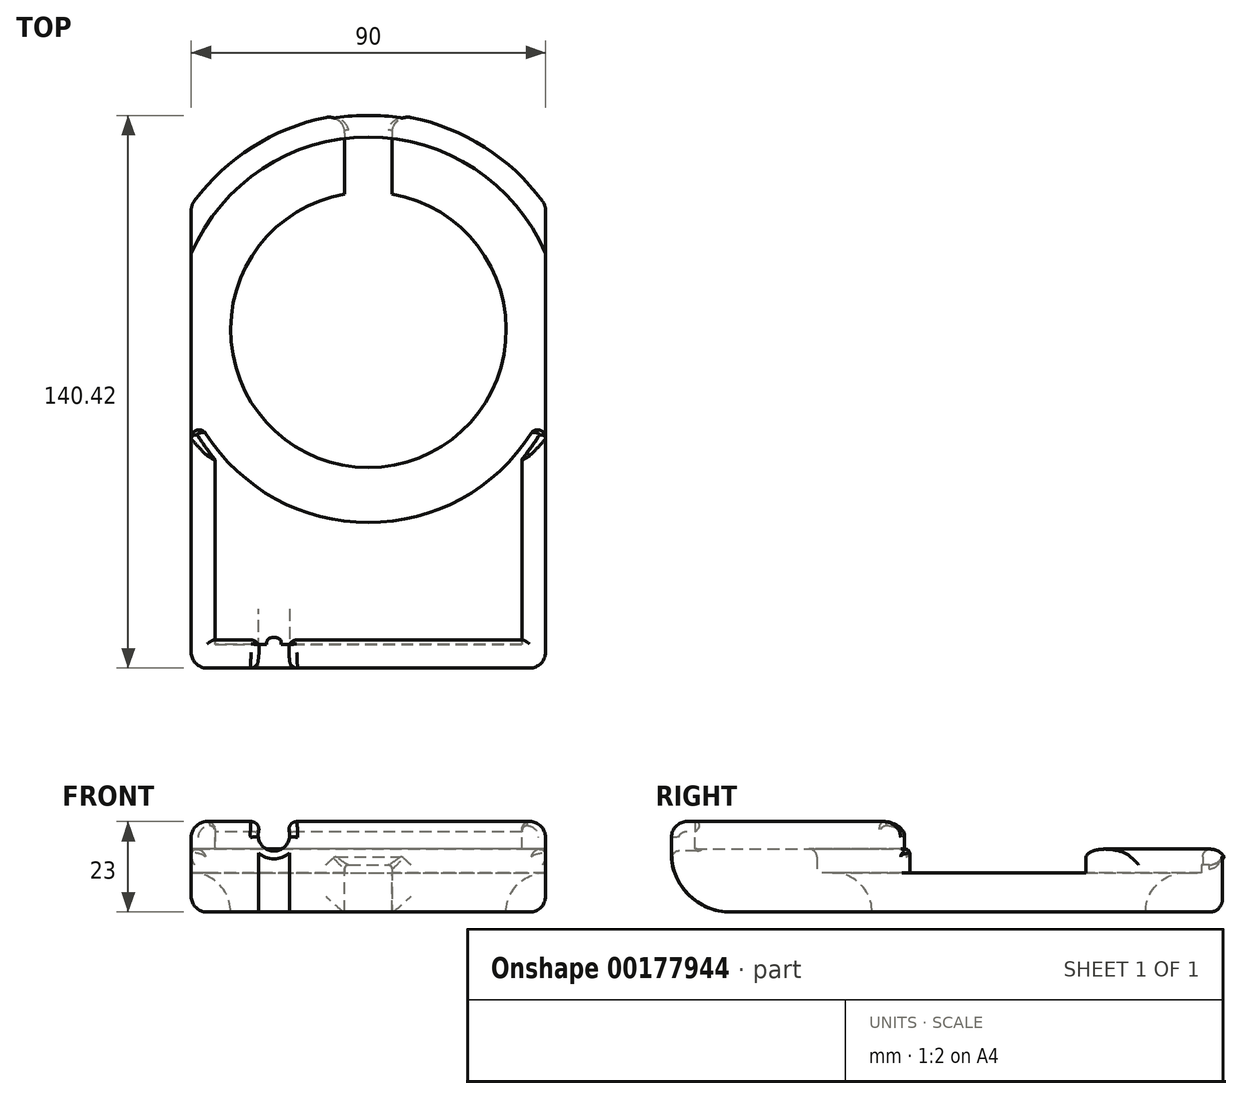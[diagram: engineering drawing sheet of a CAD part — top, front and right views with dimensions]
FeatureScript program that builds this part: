
annotation { "Feature Type Name" : "Feature", "Feature Type Description" : "" }
export const myFeature = defineFeature(function(context is Context, id is Id, definition is map)
    precondition{}
    {
        {
            var Q0;
            Q0=qCreatedBy(makeId("Top.planeOp"),FACE);
            var sketch = newSketch(context, id + "F0", { "sketchPlane" : qUnion([Q0])});
            skCircle(sketch, "E0", {"center": v(0, 0) * mm, "radius": 35 * mm});
            skLineSegment(sketch, "E1.bottom", {"start": v(45, -80) * mm, "end": v(-45, -80) * mm});
            skLineSegment(sketch, "E1.top", {"start": v(45, 80) * mm, "end": v(-45, 80) * mm});
            skLineSegment(sketch, "E1.left", {"start": v(45, -80) * mm, "end": v(45, 80) * mm});
            skLineSegment(sketch, "E1.right", {"start": v(-45, -80) * mm, "end": v(-45, 80) * mm});
            skSolve(sketch);
        }
        {
            var Q0;
            Q0 = qSketchRegion(id + "F0", true);
            extrude(context, id + "F1", {"entities" : qUnion([Q0]), "depth" : 10 * mm});
        }
        {
            var Q0;
            Q0=makeQuery(id+"F1.opExtrude","CAP_EDGE",EDGE,{"disambiguationData":[OSD([sQuery(id+"F0.wireOp",EDGE,"E0")])],"isStart":false});
            fillet(context, id + "F2", {"entities" : qUnion([Q0]), "radius" : 10 * mm, "tangentPropagation" : true, "allowEdgeOverflow" : false});
        }
        {
            var Q0;
            Q0=makeQuery(id+"F2.opFillet","SPLIT",FACE,{"disambiguationData":[OD(1.0)],"derivedFrom":makeQuery(id+"F1.opExtrude","CAP_FACE",FACE,{"disambiguationData":[OSD([sQuery(id+"F0.wireOp",EDGE,"E0"),sQuery(id+"F0.wireOp",EDGE,"E1.bottom"),sQuery(id+"F0.wireOp",EDGE,"E1.top"),sQuery(id+"F0.wireOp",EDGE,"E1.left"),sQuery(id+"F0.wireOp",EDGE,"E1.right")])],"isStart":false})});
            var sketch = newSketch(context, id + "F3", { "sketchPlane" : qUnion([Q0])});
            skCircle(sketch, "E2", {"center": v(0, 0) * mm, "radius": 49 * mm});
            skLineSegment(sketch, "E3.bottom", {"start": v(45, -80) * mm, "end": v(-45, -80) * mm});
            skLineSegment(sketch, "E3.top", {"start": v(45, 80) * mm, "end": v(-45, 80) * mm});
            skLineSegment(sketch, "E3.left", {"start": v(45, -80) * mm, "end": v(45, 80) * mm});
            skLineSegment(sketch, "E3.right", {"start": v(-45, -80) * mm, "end": v(-45, 80) * mm});
            skSolve(sketch);
        }
        {
            var Q0;
            {var subQ5=sQuery(id+"F3.wireOp",EDGE,"E3.top");Q0=makeQuery(id+"F3.imprint","IMPRINT",FACE,{"disambiguationData":[TD([[makeQuery(id+"F3.imprint","IMPRINT",EDGE,{"derivedFrom":subQ5}),1.0]])]});}
            var Q1;
            {var subQ5=sQuery(id+"F3.wireOp",EDGE,"E3.bottom");Q1=makeQuery(id+"F3.imprint","IMPRINT",FACE,{"disambiguationData":[TD([[makeQuery(id+"F3.imprint","IMPRINT",EDGE,{"derivedFrom":subQ5}),-1.0]])]});}
            extrude(context, id + "F4", {"entities" : qUnion([Q0, Q1]), "operationType" : NewBodyOperationType.ADD, "depth" : 6 * mm});
        }
        {
            var Q0;
            {var subQ0=sQuery(id+"F3.wireOp",EDGE,"E2");Q0=makeQuery(id+"F4.opExtrude","CAP_EDGE",EDGE,{"disambiguationData":[OSD([subQ0]),TDD([makeQuery(id+"F3.imprint","IMPRINT",EDGE,{"disambiguationData":[TD([[makeQuery(id+"F3.imprint","INTERSECT",VERTEX,{"disambiguationData":[OD(0.0)],"derivedFrom":[subQ0,sQuery(id+"F3.wireOp",EDGE,"E3.right")]}),1.0]])],"derivedFrom":subQ0})])],"isStart":true});}
            var Q1;
            {var subQ0=sQuery(id+"F3.wireOp",EDGE,"E2");Q1=makeQuery(id+"F4.opExtrude","CAP_EDGE",EDGE,{"disambiguationData":[OSD([subQ0]),TDD([makeQuery(id+"F3.imprint","IMPRINT",EDGE,{"disambiguationData":[TD([[makeQuery(id+"F3.imprint","INTERSECT",VERTEX,{"disambiguationData":[OD(0.0)],"derivedFrom":[subQ0,sQuery(id+"F3.wireOp",EDGE,"E3.right")]}),1.0]])],"derivedFrom":subQ0})])],"isStart":false});}
            var Q2;
            {var subQ0=sQuery(id+"F3.wireOp",EDGE,"E2");Q2=makeQuery(id+"F4.opExtrude","CAP_EDGE",EDGE,{"disambiguationData":[OSD([subQ0]),TDD([makeQuery(id+"F3.imprint","IMPRINT",EDGE,{"disambiguationData":[TD([[makeQuery(id+"F3.imprint","INTERSECT",VERTEX,{"disambiguationData":[OD(1.0)],"derivedFrom":[subQ0,sQuery(id+"F3.wireOp",EDGE,"E3.right")]}),-1.0]])],"derivedFrom":subQ0})])],"isStart":true});}
            var Q3;
            {var subQ0=sQuery(id+"F3.wireOp",EDGE,"E2");Q3=makeQuery(id+"F4.opExtrude","CAP_EDGE",EDGE,{"disambiguationData":[OSD([subQ0]),TDD([makeQuery(id+"F3.imprint","IMPRINT",EDGE,{"disambiguationData":[TD([[makeQuery(id+"F3.imprint","INTERSECT",VERTEX,{"disambiguationData":[OD(1.0)],"derivedFrom":[subQ0,sQuery(id+"F3.wireOp",EDGE,"E3.right")]}),-1.0]])],"derivedFrom":subQ0})])],"isStart":false});}
            fillet(context, id + "F5", {"entities" : qUnion([Q0, Q1, Q2, Q3]), "radius" : 2 * mm, "tangentPropagation" : true, "allowEdgeOverflow" : false});
        }
        {
            var Q0;
            Q0=makeQuery(id+"F4.opExtrude","CAP_FACE",FACE,{"disambiguationData":[OSD([sQuery(id+"F3.wireOp",EDGE,"E2"),sQuery(id+"F3.wireOp",EDGE,"E3.top"),sQuery(id+"F3.wireOp",EDGE,"E3.left"),sQuery(id+"F3.wireOp",EDGE,"E3.right")])],"isStart":false});
            var sketch = newSketch(context, id + "F6", { "sketchPlane" : qUnion([Q0])});
            skCircle(sketch, "E4", {"center": v(0, 0) * mm, "radius": 55 * mm});
            skLineSegment(sketch, "E5", {"start": v(-45, 31.62) * mm, "end": v(-45, 80) * mm});
            skLineSegment(sketch, "E6", {"start": v(-45, 80) * mm, "end": v(45, 80) * mm});
            skLineSegment(sketch, "E7", {"start": v(45, 80) * mm, "end": v(45, 31.62) * mm});
            skSolve(sketch);
        }
        {
            var Q0;
            {var subQ0=sQuery(id+"F6.wireOp",EDGE,"E5");Q0=makeQuery(id+"F6.imprint","IMPRINT",FACE,{"disambiguationData":[TD([[makeQuery(id+"F6.imprint","IMPRINT",EDGE,{"derivedFrom":subQ0}),-1.0]])]});}
            extrude(context, id + "F7", {"entities" : qUnion([Q0]), "operationType" : NewBodyOperationType.REMOVE, "endBound" : BoundingType.UP_TO_NEXT, "oppositeDirection" : true, "depth" : 25 * mm});
        }
        {
            var Q0;
            Q0=makeQuery(id+"F4.opExtrude","CAP_FACE",FACE,{"disambiguationData":[OSD([sQuery(id+"F3.wireOp",EDGE,"E2"),sQuery(id+"F3.wireOp",EDGE,"E3.bottom"),sQuery(id+"F3.wireOp",EDGE,"E3.left"),sQuery(id+"F3.wireOp",EDGE,"E3.right")])],"isStart":false});
            var sketch = newSketch(context, id + "F8", { "sketchPlane" : qUnion([Q0])});
            skLineSegment(sketch, "E8.bottom", {"start": v(39, -80) * mm, "end": v(-39, -80) * mm});
            skLineSegment(sketch, "E8.top", {"start": v(39, 80) * mm, "end": v(-39, 80) * mm});
            skLineSegment(sketch, "E8.left", {"start": v(39, -80) * mm, "end": v(39, 80) * mm});
            skLineSegment(sketch, "E8.right", {"start": v(-39, -80) * mm, "end": v(-39, 80) * mm});
            skPoint(sketch, "E8.middle", {"position": v(0, 0) * mm});
            skLineSegment(sketch, "E9.bottom", {"start": v(45, -86) * mm, "end": v(-45, -86) * mm});
            skLineSegment(sketch, "E9.top", {"start": v(45, 86) * mm, "end": v(-45, 86) * mm});
            skLineSegment(sketch, "E9.left", {"start": v(45, -86) * mm, "end": v(45, 86) * mm});
            skLineSegment(sketch, "E9.right", {"start": v(-45, -86) * mm, "end": v(-45, 86) * mm});
            skArc(sketch, "E10", {"start": v(-45, -24) * mm, "mid": v(0, -51) * mm, "end": v(45, -24) * mm});
            skSolve(sketch);
        }
        {
            var Q0;
            {var subQ1=makeQuery(id+"F4.opExtrude","CAP_EDGE",EDGE,{"disambiguationData":[OSD([sQuery(id+"F3.wireOp",EDGE,"E3.bottom")])],"isStart":false});var subQ5=sQuery(id+"F8.wireOp",EDGE,"E9.left");var subQ7=makeQuery(id+"F8.imprint","INTERSECT",VERTEX,{"derivedFrom":[subQ1,subQ5]});Q0=makeQuery(id+"F8.imprint","IMPRINT",FACE,{"disambiguationData":[TD([[makeQuery(id+"F8.imprint","IMPRINT",EDGE,{"disambiguationData":[TD([[subQ7,-1.0]])],"derivedFrom":subQ5}),1.0]])]});}
            var Q1;
            {var subQ1=makeQuery(id+"F4.opExtrude","CAP_EDGE",EDGE,{"disambiguationData":[OSD([sQuery(id+"F3.wireOp",EDGE,"E3.bottom")])],"isStart":false});var subQ5=sQuery(id+"F8.wireOp",EDGE,"E9.right");var subQ6=makeQuery(id+"F8.imprint","INTERSECT",VERTEX,{"derivedFrom":[subQ1,subQ5]});Q1=makeQuery(id+"F8.imprint","IMPRINT",FACE,{"disambiguationData":[TD([[makeQuery(id+"F8.imprint","IMPRINT",EDGE,{"disambiguationData":[TD([[subQ6,-1.0]])],"derivedFrom":subQ5}),-1.0]])]});}
            extrude(context, id + "F9", {"entities" : qUnion([Q0, Q1]), "operationType" : NewBodyOperationType.ADD, "depth" : 7 * mm});
        }
        {
            var Q0;
            Q0=qCreatedBy(makeId("Right.planeOp"),FACE);
            var sketch = newSketch(context, id + "F10", { "sketchPlane" : qUnion([Q0])});
            skLineSegment(sketch, "E11", {"start": v(-64.77, -48.06) * mm, "end": v(-70.53, -49.87) * mm});
            skLineSegment(sketch, "E12", {"start": v(-85.96, 0) * mm, "end": v(-85.96, 23) * mm});
            skLineSegment(sketch, "E13", {"start": v(-79.96, 0) * mm, "end": v(-79.96, 20.33) * mm});
            skLineSegment(sketch, "E14", {"start": v(-79.96, 0) * mm, "end": v(-85.96, 0) * mm});
            skLineSegment(sketch, "E15", {"start": v(-85.96, 23) * mm, "end": v(-77.63, 23) * mm});
            skLineSegment(sketch, "E16", {"start": v(-77.63, 23) * mm, "end": v(-79.96, 20.33) * mm});
            skSolve(sketch);
        }
        {
            var Q0;
            Q0 = qSketchRegion(id + "F10", true);
            extrude(context, id + "F11", {"entities" : qUnion([Q0]), "operationType" : NewBodyOperationType.ADD, "depth" : 45 * mm, "hasSecondDirection" : true, "secondDirectionOppositeDirection" : true, "secondDirectionDepth" : 45 * mm});
        }
        {
            var Q0;
            Q0=makeQuery(id+"F11.opExtrude","SWEPT_FACE",FACE,{"disambiguationData":[OSD([sQuery(id+"F10.wireOp",EDGE,"E12")])]});
            var sketch = newSketch(context, id + "F12", { "sketchPlane" : qUnion([Q0])});
            skCircle(sketch, "E17", {"center": v(-24, 19.53) * mm, "radius": 4 * mm});
            skSolve(sketch);
        }
        {
            var Q0;
            Q0 = qSketchRegion(id + "F12", true);
            extrude(context, id + "F13", {"entities" : qUnion([Q0]), "operationType" : NewBodyOperationType.REMOVE, "oppositeDirection" : true, "depth" : 8.5 * mm});
        }
        {
            var Q0;
            Q0=qCreatedBy(makeId("Front.planeOp"),FACE);
            var sketch = newSketch(context, id + "F14", { "sketchPlane" : qUnion([Q0])});
            skLineSegment(sketch, "E18.bottom", {"start": v(-6, 0) * mm, "end": v(6, 0) * mm});
            skLineSegment(sketch, "E18.top", {"start": v(-6, 12) * mm, "end": v(6, 12) * mm});
            skLineSegment(sketch, "E18.left", {"start": v(-6, 0) * mm, "end": v(-6, 12) * mm});
            skLineSegment(sketch, "E18.right", {"start": v(6, 0) * mm, "end": v(6, 12) * mm});
            skPoint(sketch, "E18.middle", {"position": v(0, 6) * mm});
            skSolve(sketch);
        }
        {
            var Q0;
            Q0 = qSketchRegion(id + "F14", true);
            extrude(context, id + "F15", {"entities" : qUnion([Q0]), "operationType" : NewBodyOperationType.REMOVE, "endBound" : BoundingType.THROUGH_ALL, "oppositeDirection" : true, "depth" : 25 * mm});
        }
        {
            var Q0;
            Q0=makeQuery(id+"F7.boolean.opBoolean","COPY",FACE,{"derivedFrom":makeQuery(id+"F7.opExtrude","SWEPT_FACE",FACE,{"disambiguationData":[OSD([sQuery(id+"F6.wireOp",EDGE,"E4")])]})});
            var Q1;
            Q1=makeQuery(id+"F15.boolean.opBoolean","COPY",EDGE,{"derivedFrom":makeQuery(id+"F15.opExtrude","SWEPT_EDGE",EDGE,{"disambiguationData":[OSD([sQuery(id+"F14.wireOp",EDGE,"E18.bottom"),sQuery(id+"F14.wireOp",EDGE,"E18.left")])]})});
            var Q2;
            Q2=makeQuery(id+"F15.boolean.opBoolean","COPY",EDGE,{"derivedFrom":makeQuery(id+"F15.opExtrude","SWEPT_EDGE",EDGE,{"disambiguationData":[OSD([sQuery(id+"F14.wireOp",EDGE,"E18.bottom"),sQuery(id+"F14.wireOp",EDGE,"E18.right")])]})});
            var Q3;
            Q3=makeQuery(id+"F11.boolean.opBoolean","MERGE",EDGE,{"derivedFrom":[makeQuery(id+"F1.opExtrude","CAP_EDGE",EDGE,{"disambiguationData":[OSD([sQuery(id+"F0.wireOp",EDGE,"E1.left")])],"isStart":true}),makeQuery(id+"F11.opExtrude","CAP_EDGE",EDGE,{"disambiguationData":[OSD([sQuery(id+"F10.wireOp",EDGE,"E14")])],"isStart":false})]});
            var Q4;
            Q4=makeQuery(id+"F11.boolean.opBoolean","MERGE",EDGE,{"derivedFrom":[makeQuery(id+"F1.opExtrude","CAP_EDGE",EDGE,{"disambiguationData":[OSD([sQuery(id+"F0.wireOp",EDGE,"E1.right")])],"isStart":true}),makeQuery(id+"F11.opExtrude","CAP_EDGE",EDGE,{"disambiguationData":[OSD([sQuery(id+"F10.wireOp",EDGE,"E14")])],"isStart":true})]});
            var Q5;
            Q5=makeQuery(id+"F11.opExtrude","CAP_EDGE",EDGE,{"disambiguationData":[OSD([sQuery(id+"F10.wireOp",EDGE,"E12")])],"isStart":false});
            var Q6;
            Q6=makeQuery(id+"F11.opExtrude","CAP_EDGE",EDGE,{"disambiguationData":[OSD([sQuery(id+"F10.wireOp",EDGE,"E12")])],"isStart":true});
            var Q7;
            Q7=makeQuery(id+"F11.boolean.opBoolean","MERGE",EDGE,{"derivedFrom":[makeQuery(id+"F9.opExtrude","CAP_EDGE",EDGE,{"disambiguationData":[OSD([sQuery(id+"F8.wireOp",EDGE,"E9.right")])],"isStart":false}),makeQuery(id+"F11.opExtrude","CAP_EDGE",EDGE,{"disambiguationData":[OSD([sQuery(id+"F10.wireOp",EDGE,"E15")])],"isStart":true})]});
            var Q8;
            Q8=makeQuery(id+"F11.boolean.opBoolean","MERGE",EDGE,{"derivedFrom":[makeQuery(id+"F9.opExtrude","CAP_EDGE",EDGE,{"disambiguationData":[OSD([sQuery(id+"F8.wireOp",EDGE,"E9.left")])],"isStart":false}),makeQuery(id+"F11.opExtrude","CAP_EDGE",EDGE,{"disambiguationData":[OSD([sQuery(id+"F10.wireOp",EDGE,"E15")])],"isStart":false})]});
            var Q9;
            {var subQ5=sQuery(id+"F10.wireOp",EDGE,"E12");var subQ6=sQuery(id+"F10.wireOp",EDGE,"E15");Q9=makeQuery(id+"F13.boolean.opBoolean","SPLIT",EDGE,{"disambiguationData":[TD([makeQuery(id+"F1.opExtrude","SWEPT_FACE",FACE,{"disambiguationData":[OSD([sQuery(id+"F0.wireOp",EDGE,"E1.left")])]})])],"derivedFrom":makeQuery(id+"F11.opExtrude","SWEPT_EDGE",EDGE,{"disambiguationData":[OSD([subQ5,subQ6])]})});}
            var Q10;
            {var subQ5=sQuery(id+"F10.wireOp",EDGE,"E15");var subQ6=sQuery(id+"F10.wireOp",EDGE,"E12");Q10=makeQuery(id+"F13.boolean.opBoolean","SPLIT",EDGE,{"disambiguationData":[TD([makeQuery(id+"F1.opExtrude","SWEPT_FACE",FACE,{"disambiguationData":[OSD([sQuery(id+"F0.wireOp",EDGE,"E1.right")])]})])],"derivedFrom":makeQuery(id+"F11.opExtrude","SWEPT_EDGE",EDGE,{"disambiguationData":[OSD([subQ6,subQ5])]})});}
            var Q11;
            Q11=makeQuery(id+"F13.boolean.opBoolean","COPY",EDGE,{"derivedFrom":makeQuery(id+"F13.opExtrude","CAP_EDGE",EDGE,{"disambiguationData":[OSD([sQuery(id+"F12.wireOp",EDGE,"E17")])],"isStart":true})});
            fillet(context, id + "F16", {"entities" : qUnion([Q0, Q1, Q2, Q3, Q4, Q5, Q6, Q7, Q8, Q9, Q10, Q11]), "radius" : 4 * mm, "tangentPropagation" : true, "allowEdgeOverflow" : false});
        }
        {
            var Q0;
            {var subQ0=sQuery(id+"F8.wireOp",EDGE,"E10");var subQ1=sQuery(id+"F3.wireOp",EDGE,"E3.bottom");Q0=makeQuery(id+"F13.boolean.opBoolean","INTERSECT",EDGE,{"disambiguationData":[OD(1.0)],"derivedFrom":[makeQuery(id+"F11.boolean.opBoolean","MERGE",FACE,{"derivedFrom":[makeQuery(id+"F9.opExtrude","CAP_FACE",FACE,{"disambiguationData":[OSD([subQ1,sQuery(id+"F8.wireOp",EDGE,"E8.left"),sQuery(id+"F8.wireOp",EDGE,"E9.left"),subQ0])],"isStart":false}),makeQuery(id+"F9.opExtrude","CAP_FACE",FACE,{"disambiguationData":[OSD([subQ1,sQuery(id+"F8.wireOp",EDGE,"E8.right"),sQuery(id+"F8.wireOp",EDGE,"E9.right"),subQ0])],"isStart":false}),makeQuery(id+"F11.opExtrude","SWEPT_FACE",FACE,{"disambiguationData":[OSD([sQuery(id+"F10.wireOp",EDGE,"E15")])]})]}),makeQuery(id+"F13.opExtrude","SWEPT_FACE",FACE,{"disambiguationData":[OSD([sQuery(id+"F12.wireOp",EDGE,"E17")])]})]});}
            var Q1;
            {var subQ0=sQuery(id+"F8.wireOp",EDGE,"E10");var subQ1=sQuery(id+"F3.wireOp",EDGE,"E3.bottom");Q1=makeQuery(id+"F13.boolean.opBoolean","INTERSECT",EDGE,{"disambiguationData":[OD(0.0)],"derivedFrom":[makeQuery(id+"F11.boolean.opBoolean","MERGE",FACE,{"derivedFrom":[makeQuery(id+"F9.opExtrude","CAP_FACE",FACE,{"disambiguationData":[OSD([subQ1,sQuery(id+"F8.wireOp",EDGE,"E8.left"),sQuery(id+"F8.wireOp",EDGE,"E9.left"),subQ0])],"isStart":false}),makeQuery(id+"F9.opExtrude","CAP_FACE",FACE,{"disambiguationData":[OSD([subQ1,sQuery(id+"F8.wireOp",EDGE,"E8.right"),sQuery(id+"F8.wireOp",EDGE,"E9.right"),subQ0])],"isStart":false}),makeQuery(id+"F11.opExtrude","SWEPT_FACE",FACE,{"disambiguationData":[OSD([sQuery(id+"F10.wireOp",EDGE,"E15")])]})]}),makeQuery(id+"F13.opExtrude","SWEPT_FACE",FACE,{"disambiguationData":[OSD([sQuery(id+"F12.wireOp",EDGE,"E17")])]})]});}
            var Q2;
            Q2=makeQuery(id+"F13.boolean.opBoolean","COPY",EDGE,{"derivedFrom":makeQuery(id+"F13.opExtrude","CAP_EDGE",EDGE,{"disambiguationData":[OSD([sQuery(id+"F12.wireOp",EDGE,"E17")])],"isStart":false})});
            var Q3;
            Q3=makeQuery(id+"F9.opExtrude","CAP_EDGE",EDGE,{"disambiguationData":[OSD([sQuery(id+"F8.wireOp",EDGE,"E8.left")])],"isStart":true});
            var Q4;
            Q4=makeQuery(id+"F9.opExtrude","CAP_EDGE",EDGE,{"disambiguationData":[OSD([sQuery(id+"F8.wireOp",EDGE,"E8.right")])],"isStart":true});
            var Q5;
            Q5=makeQuery(id+"F9.opExtrude","CAP_EDGE",EDGE,{"disambiguationData":[OSD([sQuery(id+"F8.wireOp",EDGE,"E8.right")])],"isStart":false});
            var Q6;
            Q6=makeQuery(id+"F9.opExtrude","CAP_EDGE",EDGE,{"disambiguationData":[OSD([sQuery(id+"F8.wireOp",EDGE,"E8.left")])],"isStart":false});
            var Q7;
            {var subQ0=sQuery(id+"F3.wireOp",EDGE,"E3.left");var subQ1=sQuery(id+"F3.wireOp",EDGE,"E2");Q7=makeQuery(id+"F5.opFillet","BLEND_EDGE",EDGE,{"blendedFrom":[makeQuery(id+"F4.opExtrude","CAP_EDGE",EDGE,{"disambiguationData":[OSD([subQ1]),TDD([makeQuery(id+"F3.imprint","IMPRINT",EDGE,{"disambiguationData":[TD([[makeQuery(id+"F3.imprint","INTERSECT",VERTEX,{"disambiguationData":[OD(1.0)],"derivedFrom":[subQ1,sQuery(id+"F3.wireOp",EDGE,"E3.right")]}),-1.0]])],"derivedFrom":subQ1})])],"isStart":false}),makeQuery(id+"F4.boolean.opBoolean","MERGE",FACE,{"derivedFrom":[makeQuery(id+"F1.opExtrude","SWEPT_FACE",FACE,{"disambiguationData":[OSD([sQuery(id+"F0.wireOp",EDGE,"E1.left")])]}),makeQuery(id+"F4.opExtrude","SWEPT_FACE",FACE,{"disambiguationData":[OSD([subQ0]),TDD([makeQuery(id+"F3.imprint","IMPRINT",EDGE,{"disambiguationData":[TD([[makeQuery(id+"F3.imprint","INTERSECT",VERTEX,{"derivedFrom":[sQuery(id+"F3.wireOp",EDGE,"E3.bottom"),subQ0]}),-1.0]])],"derivedFrom":subQ0})])]}),makeQuery(id+"F4.opExtrude","SWEPT_FACE",FACE,{"disambiguationData":[OSD([subQ0]),TDD([makeQuery(id+"F3.imprint","IMPRINT",EDGE,{"disambiguationData":[TD([[makeQuery(id+"F3.imprint","INTERSECT",VERTEX,{"derivedFrom":[sQuery(id+"F3.wireOp",EDGE,"E3.top"),subQ0]}),1.0]])],"derivedFrom":subQ0})])]})]})],"blendedInto":[makeQuery(id+"F4.boolean.opBoolean","MERGE",FACE,{"derivedFrom":[makeQuery(id+"F1.opExtrude","SWEPT_FACE",FACE,{"disambiguationData":[OSD([sQuery(id+"F0.wireOp",EDGE,"E1.left")])]}),makeQuery(id+"F4.opExtrude","SWEPT_FACE",FACE,{"disambiguationData":[OSD([subQ0]),TDD([makeQuery(id+"F3.imprint","IMPRINT",EDGE,{"disambiguationData":[TD([[makeQuery(id+"F3.imprint","INTERSECT",VERTEX,{"derivedFrom":[sQuery(id+"F3.wireOp",EDGE,"E3.bottom"),subQ0]}),-1.0]])],"derivedFrom":subQ0})])]}),makeQuery(id+"F4.opExtrude","SWEPT_FACE",FACE,{"disambiguationData":[OSD([subQ0]),TDD([makeQuery(id+"F3.imprint","IMPRINT",EDGE,{"disambiguationData":[TD([[makeQuery(id+"F3.imprint","INTERSECT",VERTEX,{"derivedFrom":[sQuery(id+"F3.wireOp",EDGE,"E3.top"),subQ0]}),1.0]])],"derivedFrom":subQ0})])]})]})]});}
            var Q8;
            {var subQ0=sQuery(id+"F3.wireOp",EDGE,"E3.right");var subQ1=sQuery(id+"F3.wireOp",EDGE,"E2");var subQ2=makeQuery(id+"F3.imprint","INTERSECT",VERTEX,{"disambiguationData":[OD(1.0)],"derivedFrom":[subQ1,subQ0]});Q8=makeQuery(id+"F5.opFillet","BLEND_EDGE",EDGE,{"blendedFrom":[makeQuery(id+"F4.opExtrude","CAP_EDGE",EDGE,{"disambiguationData":[OSD([subQ1]),TDD([makeQuery(id+"F3.imprint","IMPRINT",EDGE,{"disambiguationData":[TD([[subQ2,-1.0]])],"derivedFrom":subQ1})])],"isStart":false}),makeQuery(id+"F4.boolean.opBoolean","MERGE",FACE,{"derivedFrom":[makeQuery(id+"F1.opExtrude","SWEPT_FACE",FACE,{"disambiguationData":[OSD([sQuery(id+"F0.wireOp",EDGE,"E1.right")])]}),makeQuery(id+"F4.opExtrude","SWEPT_FACE",FACE,{"disambiguationData":[OSD([subQ0]),TDD([makeQuery(id+"F3.imprint","IMPRINT",EDGE,{"disambiguationData":[TD([[makeQuery(id+"F3.imprint","INTERSECT",VERTEX,{"derivedFrom":[sQuery(id+"F3.wireOp",EDGE,"E3.bottom"),subQ0]}),-1.0]])],"derivedFrom":subQ0})])]}),makeQuery(id+"F4.opExtrude","SWEPT_FACE",FACE,{"disambiguationData":[OSD([subQ0]),TDD([makeQuery(id+"F3.imprint","IMPRINT",EDGE,{"disambiguationData":[TD([[makeQuery(id+"F3.imprint","INTERSECT",VERTEX,{"derivedFrom":[sQuery(id+"F3.wireOp",EDGE,"E3.top"),subQ0]}),1.0]])],"derivedFrom":subQ0})])]})]})],"blendedInto":[makeQuery(id+"F4.boolean.opBoolean","MERGE",FACE,{"derivedFrom":[makeQuery(id+"F1.opExtrude","SWEPT_FACE",FACE,{"disambiguationData":[OSD([sQuery(id+"F0.wireOp",EDGE,"E1.right")])]}),makeQuery(id+"F4.opExtrude","SWEPT_FACE",FACE,{"disambiguationData":[OSD([subQ0]),TDD([makeQuery(id+"F3.imprint","IMPRINT",EDGE,{"disambiguationData":[TD([[makeQuery(id+"F3.imprint","INTERSECT",VERTEX,{"derivedFrom":[sQuery(id+"F3.wireOp",EDGE,"E3.bottom"),subQ0]}),-1.0]])],"derivedFrom":subQ0})])]}),makeQuery(id+"F4.opExtrude","SWEPT_FACE",FACE,{"disambiguationData":[OSD([subQ0]),TDD([makeQuery(id+"F3.imprint","IMPRINT",EDGE,{"disambiguationData":[TD([[makeQuery(id+"F3.imprint","INTERSECT",VERTEX,{"derivedFrom":[sQuery(id+"F3.wireOp",EDGE,"E3.top"),subQ0]}),1.0]])],"derivedFrom":subQ0})])]})]})]});}
            fillet(context, id + "F17", {"entities" : qUnion([Q0, Q1, Q2, Q3, Q4, Q5, Q6, Q7, Q8]), "radius" : 2 * mm, "tangentPropagation" : true, "allowEdgeOverflow" : false});
        }
        {
            var Q0;
            {var subQ0=sQuery(id+"F8.wireOp",EDGE,"E10");var subQ1=sQuery(id+"F3.wireOp",EDGE,"E3.left");var subQ2=sQuery(id+"F3.wireOp",EDGE,"E2");Q0=makeQuery(id+"F17.opFillet","BLEND_EDGE",EDGE,{"blendedFrom":[makeQuery(id+"F4.opExtrude","SWEPT_EDGE",EDGE,{"disambiguationData":[OSD([subQ2,subQ1]),TDD([makeQuery(id+"F3.imprint","INTERSECT",VERTEX,{"disambiguationData":[OD(1.0)],"derivedFrom":[subQ2,subQ1]})])]}),makeQuery(id+"F9.opExtrude","SWEPT_FACE",FACE,{"disambiguationData":[OSD([subQ0]),TDD([makeQuery(id+"F8.imprint","IMPRINT",EDGE,{"disambiguationData":[TD([[makeQuery(id+"F8.imprint","INTERSECT",VERTEX,{"derivedFrom":[sQuery(id+"F8.wireOp",EDGE,"E9.left"),subQ0]}),-1.0]])],"derivedFrom":subQ0})])]})],"blendedInto":[makeQuery(id+"F9.opExtrude","SWEPT_FACE",FACE,{"disambiguationData":[OSD([subQ0]),TDD([makeQuery(id+"F8.imprint","IMPRINT",EDGE,{"disambiguationData":[TD([[makeQuery(id+"F8.imprint","INTERSECT",VERTEX,{"derivedFrom":[sQuery(id+"F8.wireOp",EDGE,"E9.left"),subQ0]}),-1.0]])],"derivedFrom":subQ0})])]})]});}
            var Q1;
            {var subQ0=sQuery(id+"F8.wireOp",EDGE,"E10");var subQ1=sQuery(id+"F3.wireOp",EDGE,"E3.right");var subQ2=sQuery(id+"F3.wireOp",EDGE,"E2");Q1=makeQuery(id+"F17.opFillet","BLEND_EDGE",EDGE,{"blendedFrom":[makeQuery(id+"F4.opExtrude","SWEPT_EDGE",EDGE,{"disambiguationData":[OSD([subQ2,subQ1]),TDD([makeQuery(id+"F3.imprint","INTERSECT",VERTEX,{"disambiguationData":[OD(1.0)],"derivedFrom":[subQ2,subQ1]})])]}),makeQuery(id+"F9.opExtrude","SWEPT_FACE",FACE,{"disambiguationData":[OSD([subQ0]),TDD([makeQuery(id+"F8.imprint","IMPRINT",EDGE,{"disambiguationData":[TD([[makeQuery(id+"F8.imprint","INTERSECT",VERTEX,{"derivedFrom":[sQuery(id+"F8.wireOp",EDGE,"E9.right"),subQ0]}),1.0]])],"derivedFrom":subQ0})])]})],"blendedInto":[makeQuery(id+"F9.opExtrude","SWEPT_FACE",FACE,{"disambiguationData":[OSD([subQ0]),TDD([makeQuery(id+"F8.imprint","IMPRINT",EDGE,{"disambiguationData":[TD([[makeQuery(id+"F8.imprint","INTERSECT",VERTEX,{"derivedFrom":[sQuery(id+"F8.wireOp",EDGE,"E9.right"),subQ0]}),1.0]])],"derivedFrom":subQ0})])]})]});}
            var Q2;
            {var subQ0=sQuery(id+"F3.wireOp",EDGE,"E3.right");var subQ1=sQuery(id+"F3.wireOp",EDGE,"E2");var subQ2=makeQuery(id+"F3.imprint","INTERSECT",VERTEX,{"disambiguationData":[OD(1.0)],"derivedFrom":[subQ1,subQ0]});Q2=makeQuery(id+"F17.opFillet","BLEND_EDGE",EDGE,{"blendedFrom":[makeQuery(id+"F4.opExtrude","SWEPT_EDGE",EDGE,{"disambiguationData":[OSD([subQ1,subQ0]),TDD([subQ2])]}),makeQuery(id+"F5.opFillet","BLEND_FACE",FACE,{"disambiguationData":[OSD([subQ1]),TDD([makeQuery(id+"F4.opExtrude","CAP_EDGE",EDGE,{"disambiguationData":[OSD([subQ1]),TDD([makeQuery(id+"F3.imprint","IMPRINT",EDGE,{"disambiguationData":[TD([[subQ2,-1.0]])],"derivedFrom":subQ1})])],"isStart":false})])]})],"blendedInto":[makeQuery(id+"F5.opFillet","BLEND_FACE",FACE,{"disambiguationData":[OSD([subQ1]),TDD([makeQuery(id+"F4.opExtrude","CAP_EDGE",EDGE,{"disambiguationData":[OSD([subQ1]),TDD([makeQuery(id+"F3.imprint","IMPRINT",EDGE,{"disambiguationData":[TD([[subQ2,-1.0]])],"derivedFrom":subQ1})])],"isStart":false})])]})]});}
            var Q3;
            {var subQ0=sQuery(id+"F3.wireOp",EDGE,"E2");var subQ1=sQuery(id+"F3.wireOp",EDGE,"E3.left");var subQ2=makeQuery(id+"F3.imprint","INTERSECT",VERTEX,{"disambiguationData":[OD(1.0)],"derivedFrom":[subQ0,subQ1]});Q3=makeQuery(id+"F17.opFillet","BLEND_EDGE",EDGE,{"blendedFrom":[makeQuery(id+"F4.opExtrude","SWEPT_EDGE",EDGE,{"disambiguationData":[OSD([subQ0,subQ1]),TDD([subQ2])]}),makeQuery(id+"F5.opFillet","BLEND_FACE",FACE,{"disambiguationData":[OSD([subQ0]),TDD([makeQuery(id+"F4.opExtrude","CAP_EDGE",EDGE,{"disambiguationData":[OSD([subQ0]),TDD([makeQuery(id+"F3.imprint","IMPRINT",EDGE,{"disambiguationData":[TD([[makeQuery(id+"F3.imprint","INTERSECT",VERTEX,{"disambiguationData":[OD(1.0)],"derivedFrom":[subQ0,sQuery(id+"F3.wireOp",EDGE,"E3.right")]}),-1.0]])],"derivedFrom":subQ0})])],"isStart":false})])]})],"blendedInto":[makeQuery(id+"F5.opFillet","BLEND_FACE",FACE,{"disambiguationData":[OSD([subQ0]),TDD([makeQuery(id+"F4.opExtrude","CAP_EDGE",EDGE,{"disambiguationData":[OSD([subQ0]),TDD([makeQuery(id+"F3.imprint","IMPRINT",EDGE,{"disambiguationData":[TD([[makeQuery(id+"F3.imprint","INTERSECT",VERTEX,{"disambiguationData":[OD(1.0)],"derivedFrom":[subQ0,sQuery(id+"F3.wireOp",EDGE,"E3.right")]}),-1.0]])],"derivedFrom":subQ0})])],"isStart":false})])]})]});}
            var Q4;
            {var subQ0=sQuery(id+"F8.wireOp",EDGE,"E10");var subQ1=sQuery(id+"F8.wireOp",EDGE,"E9.right");Q4=makeQuery(id+"F16.opFillet","BLEND_EDGE",EDGE,{"blendedFrom":[makeQuery(id+"F11.boolean.opBoolean","MERGE",EDGE,{"derivedFrom":[makeQuery(id+"F9.opExtrude","CAP_EDGE",EDGE,{"disambiguationData":[OSD([subQ1])],"isStart":false}),makeQuery(id+"F11.opExtrude","CAP_EDGE",EDGE,{"disambiguationData":[OSD([sQuery(id+"F10.wireOp",EDGE,"E15")])],"isStart":true})]}),makeQuery(id+"F9.opExtrude","SWEPT_FACE",FACE,{"disambiguationData":[OSD([subQ0]),TDD([makeQuery(id+"F8.imprint","IMPRINT",EDGE,{"disambiguationData":[TD([[makeQuery(id+"F8.imprint","INTERSECT",VERTEX,{"derivedFrom":[subQ1,subQ0]}),1.0]])],"derivedFrom":subQ0})])]})],"blendedInto":[makeQuery(id+"F9.opExtrude","SWEPT_FACE",FACE,{"disambiguationData":[OSD([subQ0]),TDD([makeQuery(id+"F8.imprint","IMPRINT",EDGE,{"disambiguationData":[TD([[makeQuery(id+"F8.imprint","INTERSECT",VERTEX,{"derivedFrom":[subQ1,subQ0]}),1.0]])],"derivedFrom":subQ0})])]})]});}
            var Q5;
            {var subQ0=sQuery(id+"F8.wireOp",EDGE,"E10");var subQ1=sQuery(id+"F8.wireOp",EDGE,"E9.left");Q5=makeQuery(id+"F16.opFillet","BLEND_EDGE",EDGE,{"blendedFrom":[makeQuery(id+"F11.boolean.opBoolean","MERGE",EDGE,{"derivedFrom":[makeQuery(id+"F9.opExtrude","CAP_EDGE",EDGE,{"disambiguationData":[OSD([subQ1])],"isStart":false}),makeQuery(id+"F11.opExtrude","CAP_EDGE",EDGE,{"disambiguationData":[OSD([sQuery(id+"F10.wireOp",EDGE,"E15")])],"isStart":false})]}),makeQuery(id+"F9.opExtrude","SWEPT_FACE",FACE,{"disambiguationData":[OSD([subQ0]),TDD([makeQuery(id+"F8.imprint","IMPRINT",EDGE,{"disambiguationData":[TD([[makeQuery(id+"F8.imprint","INTERSECT",VERTEX,{"derivedFrom":[subQ1,subQ0]}),-1.0]])],"derivedFrom":subQ0})])]})],"blendedInto":[makeQuery(id+"F9.opExtrude","SWEPT_FACE",FACE,{"disambiguationData":[OSD([subQ0]),TDD([makeQuery(id+"F8.imprint","IMPRINT",EDGE,{"disambiguationData":[TD([[makeQuery(id+"F8.imprint","INTERSECT",VERTEX,{"derivedFrom":[subQ1,subQ0]}),-1.0]])],"derivedFrom":subQ0})])]})]});}
            var Q6;
            {var subQ0=sQuery(id+"F10.wireOp",EDGE,"E15");var subQ3=sQuery(id+"F8.wireOp",EDGE,"E8.left");var subQ4=sQuery(id+"F10.wireOp",EDGE,"E16");Q6=makeQuery(id+"F13.boolean.opBoolean","SPLIT",EDGE,{"disambiguationData":[TD([makeQuery(id+"F9.opExtrude","SWEPT_FACE",FACE,{"disambiguationData":[OSD([subQ3])]})])],"derivedFrom":makeQuery(id+"F11.opExtrude","SWEPT_EDGE",EDGE,{"disambiguationData":[OSD([subQ0,subQ4])]})});}
            var Q7;
            {var subQ0=sQuery(id+"F10.wireOp",EDGE,"E15");var subQ2=sQuery(id+"F8.wireOp",EDGE,"E8.right");var subQ4=sQuery(id+"F10.wireOp",EDGE,"E16");Q7=makeQuery(id+"F13.boolean.opBoolean","SPLIT",EDGE,{"disambiguationData":[TD([makeQuery(id+"F9.opExtrude","SWEPT_FACE",FACE,{"disambiguationData":[OSD([subQ2])]})])],"derivedFrom":makeQuery(id+"F11.opExtrude","SWEPT_EDGE",EDGE,{"disambiguationData":[OSD([subQ0,subQ4])]})});}
            var Q8;
            Q8=makeQuery(id+"F15.boolean.opBoolean","COPY",EDGE,{"derivedFrom":makeQuery(id+"F15.opExtrude","SWEPT_EDGE",EDGE,{"disambiguationData":[OSD([sQuery(id+"F14.wireOp",EDGE,"E18.top"),sQuery(id+"F14.wireOp",EDGE,"E18.right")])]})});
            var Q9;
            Q9=makeQuery(id+"F15.boolean.opBoolean","COPY",EDGE,{"derivedFrom":makeQuery(id+"F15.opExtrude","SWEPT_EDGE",EDGE,{"disambiguationData":[OSD([sQuery(id+"F14.wireOp",EDGE,"E18.top"),sQuery(id+"F14.wireOp",EDGE,"E18.left")])]})});
            fillet(context, id + "F18", {"entities" : qUnion([Q0, Q1, Q2, Q3, Q4, Q5, Q6, Q7, Q8, Q9]), "radius" : 1 * mm, "tangentPropagation" : true, "allowEdgeOverflow" : false});
        }
        {
            var Q0;
            Q0=makeQuery(id+"F11.opExtrude","SWEPT_EDGE",EDGE,{"disambiguationData":[OSD([sQuery(id+"F10.wireOp",EDGE,"E12"),sQuery(id+"F10.wireOp",EDGE,"E14")])]});
            fillet(context, id + "F19", {"entities" : qUnion([Q0]), "radius" : 15 * mm, "tangentPropagation" : true, "allowEdgeOverflow" : false});
        }
    });
